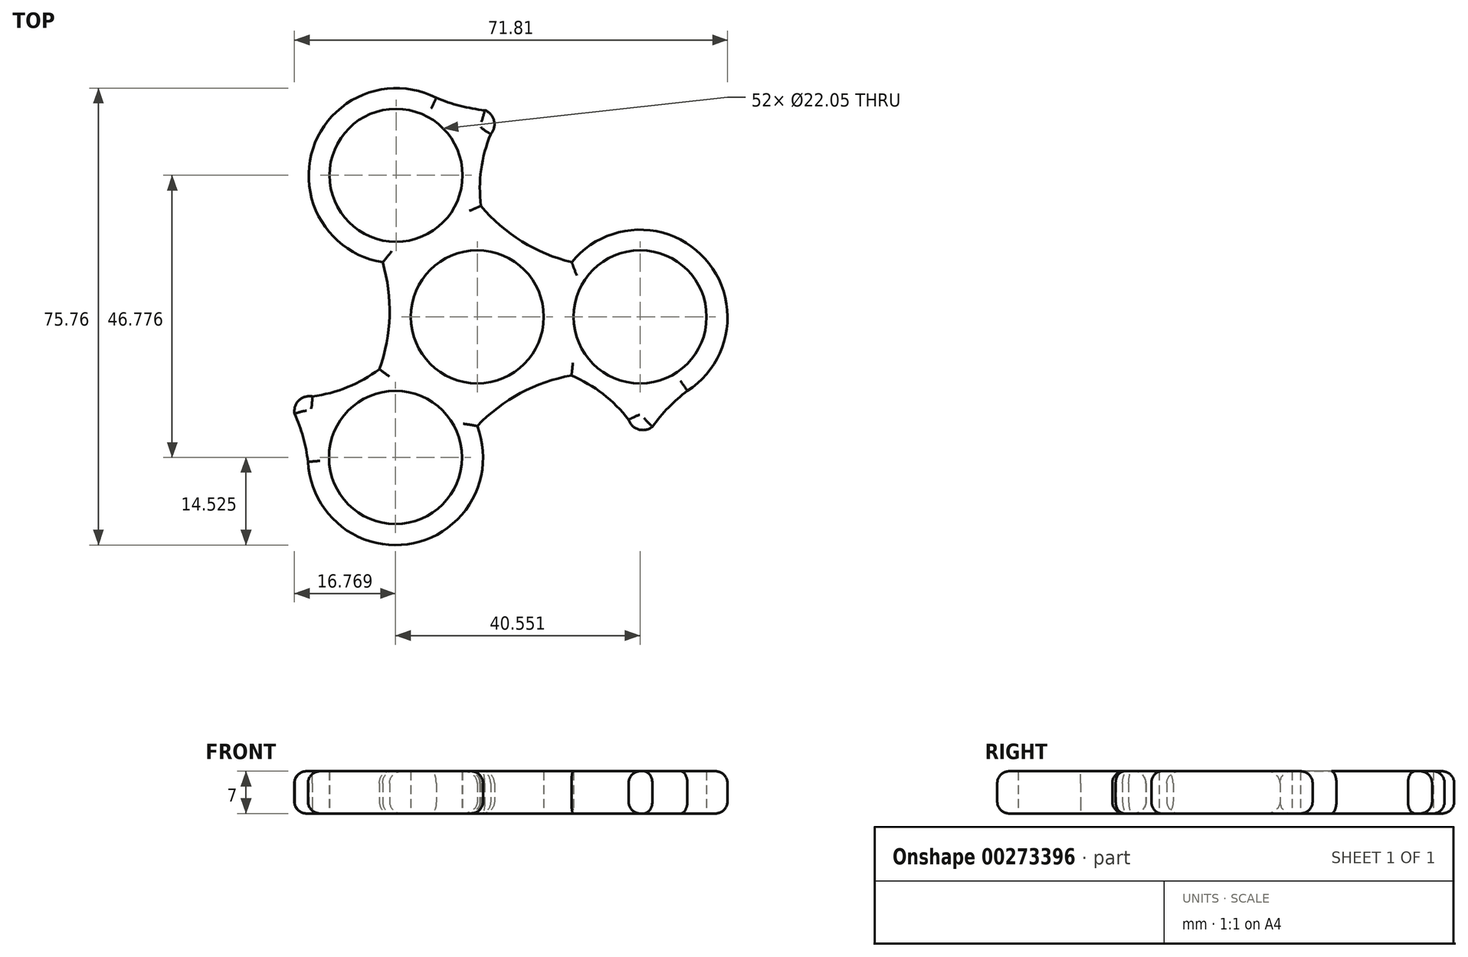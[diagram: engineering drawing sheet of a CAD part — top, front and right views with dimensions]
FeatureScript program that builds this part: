
annotation { "Feature Type Name" : "Feature", "Feature Type Description" : "" }
export const myFeature = defineFeature(function(context is Context, id is Id, definition is map)
    precondition{}
    {
        {
            var Q0;
            Q0=qCreatedBy(makeId("Top.planeOp"),FACE);
            var sketch = newSketch(context, id + "F0", { "sketchPlane" : qUnion([Q0])});
            skCircle(sketch, "E0", {"center": v(0, 0) * mm, "radius": 11.03 * mm});
            skCircle(sketch, "E1", {"center": v(27, 0) * mm, "radius": 11.03 * mm});
            skPoint(sketch, "E2.orphan", {"position": v(-24.95, -16.35) * mm});
            skCircle(sketch, "E3.1.0", {"center": v(-13.47, 23.46) * mm, "radius": 11.03 * mm});
            skCircle(sketch, "E3.2.0", {"center": v(-13.55, -23.31) * mm, "radius": 11.03 * mm});
            skArc(sketch, "E3.2.1", {"start": v(-28.06, -24.04) * mm, "mid": v(-9.44, -37.25) * mm, "end": v(-0.97, -16.05) * mm});
            skArc(sketch, "E3.2.2", {"start": v(-28.06, -24.04) * mm, "mid": v(-28.87, -19.96) * mm, "end": v(-30.29, -16.04) * mm});
            skArc(sketch, "E3.2.3", {"start": v(-27.33, -13.2) * mm, "mid": v(-20.15, -11.06) * mm, "end": v(-14, -6.78) * mm});
            skArc(sketch, "E3.2.4", {"start": v(-27.33, -13.2) * mm, "mid": v(-29.56, -13.85) * mm, "end": v(-30.29, -16.04) * mm});
            skPoint(sketch, "E3.center", {"position": v(0, 0.05) * mm});
            skArc(sketch, "E4.0", {"start": v(-16.23, -8.67) * mm, "mid": v(-14.53, 1.1) * mm, "end": v(-16.28, 10.85) * mm});
            skArc(sketch, "E5.1.0", {"start": v(25.1, -17.07) * mm, "mid": v(26.77, -18.67) * mm, "end": v(29.04, -18.21) * mm});
            skArc(sketch, "E5.1.1", {"start": v(34.85, -12.28) * mm, "mid": v(31.72, -15.03) * mm, "end": v(29.04, -18.21) * mm});
            skArc(sketch, "E5.1.2", {"start": v(34.85, -12.28) * mm, "mid": v(36.98, 10.45) * mm, "end": v(14.38, 7.18) * mm});
            skArc(sketch, "E5.1.3", {"start": v(25.1, -17.07) * mm, "mid": v(19.66, -11.92) * mm, "end": v(12.87, -8.74) * mm});
            skArc(sketch, "E5.1.4", {"start": v(15.63, -9.72) * mm, "mid": v(6.32, -13.13) * mm, "end": v(-1.26, -19.53) * mm});
            skArc(sketch, "E5.2.0", {"start": v(2.23, 30.27) * mm, "mid": v(2.79, 32.52) * mm, "end": v(1.25, 34.25) * mm});
            skArc(sketch, "E5.2.1", {"start": v(-6.8, 36.32) * mm, "mid": v(-2.85, 34.98) * mm, "end": v(1.25, 34.25) * mm});
            skArc(sketch, "E5.2.2", {"start": v(-6.8, 36.32) * mm, "mid": v(-27.54, 26.8) * mm, "end": v(-13.4, 8.87) * mm});
            skArc(sketch, "E5.2.3", {"start": v(2.23, 30.27) * mm, "mid": v(0.5, 22.98) * mm, "end": v(1.14, 15.52) * mm});
            skArc(sketch, "E5.2.4", {"start": v(0.6, 18.4) * mm, "mid": v(8.21, 12.04) * mm, "end": v(17.54, 8.68) * mm});
            skCircle(sketch, "E6", {"center": v(0, 0) * mm, "radius": 41.5 * mm, "construction": true});
            skSolve(sketch);
        }
        {
            var Q0;
            Q0=makeQuery(id+"F0.imprint","IMPRINT",FACE,{"disambiguationData":[TD([[makeQuery(id+"F0.imprint","IMPRINT",EDGE,{"derivedFrom":sQuery(id+"F0.wireOp",EDGE,"E0")}),-1.0]])]});
            extrude(context, id + "F1", {"entities" : qUnion([Q0]), "depth" : 7 * mm});
        }
        {
            var Q0;
            Q0=makeQuery(id+"F1.opExtrude","CAP_EDGE",EDGE,{"disambiguationData":[OSD([sQuery(id+"F0.wireOp",EDGE,"2c41e8ea-b216-4982-985e-4cea36fc87c6.1.2")])],"isStart":true});
            var Q1;
            Q1=makeQuery(id+"F1.opExtrude","CAP_EDGE",EDGE,{"disambiguationData":[OSD([sQuery(id+"F0.wireOp",EDGE,"jCiB0JCp-XQ0B-x5m0-Kedy-DZMXEMae4YiA")])],"isStart":true});
            var Q2;
            Q2=makeQuery(id+"F1.opExtrude","CAP_EDGE",EDGE,{"disambiguationData":[OSD([sQuery(id+"F0.wireOp",EDGE,"8rKnusNR-KdCl-6pd1-ZRWQ-f5KsOQsDNK9e")])],"isStart":true});
            var Q3;
            Q3=makeQuery(id+"F1.opExtrude","CAP_EDGE",EDGE,{"disambiguationData":[OSD([sQuery(id+"F0.wireOp",EDGE,"e85625f6-0f73-4f70-b7ad-6b2c52379fcd.2.0")])],"isStart":true});
            var Q4;
            Q4=makeQuery(id+"F1.opExtrude","CAP_EDGE",EDGE,{"disambiguationData":[OSD([sQuery(id+"F0.wireOp",EDGE,"e85625f6-0f73-4f70-b7ad-6b2c52379fcd.1.0")])],"isStart":true});
            var Q5;
            Q5=makeQuery(id+"F1.opExtrude","CAP_EDGE",EDGE,{"disambiguationData":[OSD([sQuery(id+"F0.wireOp",EDGE,"2c41e8ea-b216-4982-985e-4cea36fc87c6.2.2")])],"isStart":true});
            var Q6;
            Q6=makeQuery(id+"F1.opExtrude","CAP_EDGE",EDGE,{"disambiguationData":[OSD([sQuery(id+"F0.wireOp",EDGE,"jCiB0JCp-XQ0B-x5m0-Kedy-DZMXEMae4YiA")])],"isStart":false});
            var Q7;
            Q7=makeQuery(id+"F1.opExtrude","CAP_EDGE",EDGE,{"disambiguationData":[OSD([sQuery(id+"F0.wireOp",EDGE,"2c41e8ea-b216-4982-985e-4cea36fc87c6.1.2")])],"isStart":false});
            var Q8;
            Q8=makeQuery(id+"F1.opExtrude","CAP_EDGE",EDGE,{"disambiguationData":[OSD([sQuery(id+"F0.wireOp",EDGE,"e85625f6-0f73-4f70-b7ad-6b2c52379fcd.2.0")])],"isStart":false});
            var Q9;
            Q9=makeQuery(id+"F1.opExtrude","CAP_EDGE",EDGE,{"disambiguationData":[OSD([sQuery(id+"F0.wireOp",EDGE,"8rKnusNR-KdCl-6pd1-ZRWQ-f5KsOQsDNK9e")])],"isStart":false});
            var Q10;
            Q10=makeQuery(id+"F1.opExtrude","CAP_EDGE",EDGE,{"disambiguationData":[OSD([sQuery(id+"F0.wireOp",EDGE,"2c41e8ea-b216-4982-985e-4cea36fc87c6.2.2")])],"isStart":false});
            var Q11;
            Q11=makeQuery(id+"F1.opExtrude","CAP_EDGE",EDGE,{"disambiguationData":[OSD([sQuery(id+"F0.wireOp",EDGE,"qkignPZE-vKHs-Vw8X-w2Nq-P10X6wtjNAuJ")])],"isStart":false});
            var Q12;
            Q12=makeQuery(id+"F1.opExtrude","CAP_EDGE",EDGE,{"disambiguationData":[OSD([sQuery(id+"F0.wireOp",EDGE,"a09d2315-2299-4be2-bcc0-b27aebac17a9.1.1")])],"isStart":false});
            var Q13;
            Q13=makeQuery(id+"F1.opExtrude","CAP_EDGE",EDGE,{"disambiguationData":[OSD([sQuery(id+"F0.wireOp",EDGE,"a09d2315-2299-4be2-bcc0-b27aebac17a9.2.1")])],"isStart":false});
            var Q14;
            Q14=makeQuery(id+"F1.opExtrude","CAP_EDGE",EDGE,{"disambiguationData":[OSD([sQuery(id+"F0.wireOp",EDGE,"a09d2315-2299-4be2-bcc0-b27aebac17a9.2.0")])],"isStart":false});
            var Q15;
            Q15=makeQuery(id+"F1.opExtrude","CAP_EDGE",EDGE,{"disambiguationData":[OSD([sQuery(id+"F0.wireOp",EDGE,"7JYrFIuE-K7Xn-0Jy4-bwcr-O0BEukw54Et5")])],"isStart":false});
            var Q16;
            Q16=makeQuery(id+"F1.opExtrude","CAP_EDGE",EDGE,{"disambiguationData":[OSD([sQuery(id+"F0.wireOp",EDGE,"d141c151-67c0-49ed-b5f6-7262cdf8d574.2.2")])],"isStart":false});
            var Q17;
            Q17=makeQuery(id+"F1.opExtrude","CAP_EDGE",EDGE,{"disambiguationData":[OSD([sQuery(id+"F0.wireOp",EDGE,"a09d2315-2299-4be2-bcc0-b27aebac17a9.1.0")])],"isStart":false});
            var Q18;
            Q18=makeQuery(id+"F1.opExtrude","CAP_EDGE",EDGE,{"disambiguationData":[OSD([sQuery(id+"F0.wireOp",EDGE,"vcM62SHT-zkDI-DuHv-aWbG-MSvfoTBMthVj")])],"isStart":false});
            var Q19;
            Q19=makeQuery(id+"F1.opExtrude","CAP_EDGE",EDGE,{"disambiguationData":[OSD([sQuery(id+"F0.wireOp",EDGE,"d141c151-67c0-49ed-b5f6-7262cdf8d574.1.2")])],"isStart":false});
            var Q20;
            Q20=makeQuery(id+"F1.opExtrude","CAP_EDGE",EDGE,{"disambiguationData":[OSD([sQuery(id+"F0.wireOp",EDGE,"e85625f6-0f73-4f70-b7ad-6b2c52379fcd.1.0")])],"isStart":false});
            var Q21;
            Q21=makeQuery(id+"F1.opExtrude","CAP_EDGE",EDGE,{"disambiguationData":[OSD([sQuery(id+"F0.wireOp",EDGE,"7JYrFIuE-K7Xn-0Jy4-bwcr-O0BEukw54Et5")])],"isStart":true});
            var Q22;
            Q22=makeQuery(id+"F1.opExtrude","CAP_EDGE",EDGE,{"disambiguationData":[OSD([sQuery(id+"F0.wireOp",EDGE,"qkignPZE-vKHs-Vw8X-w2Nq-P10X6wtjNAuJ")])],"isStart":true});
            var Q23;
            Q23=makeQuery(id+"F1.opExtrude","CAP_EDGE",EDGE,{"disambiguationData":[OSD([sQuery(id+"F0.wireOp",EDGE,"a09d2315-2299-4be2-bcc0-b27aebac17a9.2.0")])],"isStart":true});
            var Q24;
            Q24=makeQuery(id+"F1.opExtrude","CAP_EDGE",EDGE,{"disambiguationData":[OSD([sQuery(id+"F0.wireOp",EDGE,"a09d2315-2299-4be2-bcc0-b27aebac17a9.2.1")])],"isStart":true});
            var Q25;
            Q25=makeQuery(id+"F1.opExtrude","CAP_EDGE",EDGE,{"disambiguationData":[OSD([sQuery(id+"F0.wireOp",EDGE,"a09d2315-2299-4be2-bcc0-b27aebac17a9.1.1")])],"isStart":true});
            var Q26;
            Q26=makeQuery(id+"F1.opExtrude","CAP_EDGE",EDGE,{"disambiguationData":[OSD([sQuery(id+"F0.wireOp",EDGE,"a09d2315-2299-4be2-bcc0-b27aebac17a9.1.0")])],"isStart":true});
            var Q27;
            Q27=makeQuery(id+"F1.opExtrude","CAP_EDGE",EDGE,{"disambiguationData":[OSD([sQuery(id+"F0.wireOp",EDGE,"vcM62SHT-zkDI-DuHv-aWbG-MSvfoTBMthVj")])],"isStart":true});
            var Q28;
            Q28=makeQuery(id+"F1.opExtrude","CAP_EDGE",EDGE,{"disambiguationData":[OSD([sQuery(id+"F0.wireOp",EDGE,"EyXljZKZ-RbeY-ZyGO-U8lE-6hOu3Im0BXS0")])],"isStart":true});
            var Q29;
            Q29=makeQuery(id+"F1.opExtrude","CAP_EDGE",EDGE,{"disambiguationData":[OSD([sQuery(id+"F0.wireOp",EDGE,"247ecdd3-580a-4f05-8964-3e7654aa62d4.1.0")])],"isStart":true});
            var Q30;
            Q30=makeQuery(id+"F1.opExtrude","CAP_EDGE",EDGE,{"disambiguationData":[OSD([sQuery(id+"F0.wireOp",EDGE,"247ecdd3-580a-4f05-8964-3e7654aa62d4.2.0")])],"isStart":true});
            var Q31;
            Q31=makeQuery(id+"F1.opExtrude","CAP_EDGE",EDGE,{"disambiguationData":[OSD([sQuery(id+"F0.wireOp",EDGE,"247ecdd3-580a-4f05-8964-3e7654aa62d4.2.0")])],"isStart":false});
            var Q32;
            Q32=makeQuery(id+"F1.opExtrude","CAP_EDGE",EDGE,{"disambiguationData":[OSD([sQuery(id+"F0.wireOp",EDGE,"EyXljZKZ-RbeY-ZyGO-U8lE-6hOu3Im0BXS0")])],"isStart":false});
            var Q33;
            Q33=makeQuery(id+"F1.opExtrude","CAP_EDGE",EDGE,{"disambiguationData":[OSD([sQuery(id+"F0.wireOp",EDGE,"247ecdd3-580a-4f05-8964-3e7654aa62d4.1.0")])],"isStart":false});
            var Q34;
            Q34=makeQuery(id+"F1.opExtrude","CAP_EDGE",EDGE,{"disambiguationData":[OSD([sQuery(id+"F0.wireOp",EDGE,"ed2d72a4-419b-47cf-ace9-9678367d7267.2.0")])],"isStart":false});
            var Q35;
            Q35=makeQuery(id+"F1.opExtrude","CAP_EDGE",EDGE,{"disambiguationData":[OSD([sQuery(id+"F0.wireOp",EDGE,"ed2d72a4-419b-47cf-ace9-9678367d7267.1.0")])],"isStart":false});
            var Q36;
            Q36=makeQuery(id+"F1.opExtrude","CAP_EDGE",EDGE,{"disambiguationData":[OSD([sQuery(id+"F0.wireOp",EDGE,"ed2d72a4-419b-47cf-ace9-9678367d7267.1.1")])],"isStart":false});
            var Q37;
            Q37=makeQuery(id+"F1.opExtrude","CAP_EDGE",EDGE,{"disambiguationData":[OSD([sQuery(id+"F0.wireOp",EDGE,"weM6L15f-GAZl-oho3-8Uek-PDMmfMEMd7Oe")])],"isStart":false});
            var Q38;
            Q38=makeQuery(id+"F1.opExtrude","CAP_EDGE",EDGE,{"disambiguationData":[OSD([sQuery(id+"F0.wireOp",EDGE,"ed2d72a4-419b-47cf-ace9-9678367d7267.2.2")])],"isStart":false});
            var Q39;
            Q39=makeQuery(id+"F1.opExtrude","CAP_EDGE",EDGE,{"disambiguationData":[OSD([sQuery(id+"F0.wireOp",EDGE,"ed2d72a4-419b-47cf-ace9-9678367d7267.1.1")])],"isStart":true});
            var Q40;
            Q40=makeQuery(id+"F1.opExtrude","CAP_EDGE",EDGE,{"disambiguationData":[OSD([sQuery(id+"F0.wireOp",EDGE,"ed2d72a4-419b-47cf-ace9-9678367d7267.1.0")])],"isStart":true});
            var Q41;
            Q41=makeQuery(id+"F1.opExtrude","CAP_EDGE",EDGE,{"disambiguationData":[OSD([sQuery(id+"F0.wireOp",EDGE,"ed2d72a4-419b-47cf-ace9-9678367d7267.1.2")])],"isStart":true});
            var Q42;
            Q42=makeQuery(id+"F1.opExtrude","CAP_EDGE",EDGE,{"disambiguationData":[OSD([sQuery(id+"F0.wireOp",EDGE,"weM6L15f-GAZl-oho3-8Uek-PDMmfMEMd7Oe")])],"isStart":true});
            var Q43;
            Q43=makeQuery(id+"F1.opExtrude","CAP_EDGE",EDGE,{"disambiguationData":[OSD([sQuery(id+"F0.wireOp",EDGE,"ed2d72a4-419b-47cf-ace9-9678367d7267.2.0")])],"isStart":true});
            var Q44;
            Q44=makeQuery(id+"F1.opExtrude","CAP_EDGE",EDGE,{"disambiguationData":[OSD([sQuery(id+"F0.wireOp",EDGE,"ed2d72a4-419b-47cf-ace9-9678367d7267.2.2")])],"isStart":true});
            var Q45;
            Q45=makeQuery(id+"F1.opExtrude","CAP_EDGE",EDGE,{"disambiguationData":[OSD([sQuery(id+"F0.wireOp",EDGE,"ed2d72a4-419b-47cf-ace9-9678367d7267.1.2")])],"isStart":false});
            var Q46;
            Q46=makeQuery(id+"F1.opExtrude","CAP_EDGE",EDGE,{"disambiguationData":[OSD([sQuery(id+"F0.wireOp",EDGE,"E3.1.1")])],"isStart":true});
            var Q47;
            Q47=makeQuery(id+"F1.opExtrude","CAP_EDGE",EDGE,{"disambiguationData":[OSD([sQuery(id+"F0.wireOp",EDGE,"E3.1.3")])],"isStart":true});
            var Q48;
            Q48=makeQuery(id+"F1.opExtrude","CAP_EDGE",EDGE,{"disambiguationData":[OSD([sQuery(id+"F0.wireOp",EDGE,"E3.1.4")])],"isStart":true});
            var Q49;
            Q49=makeQuery(id+"F1.opExtrude","CAP_EDGE",EDGE,{"disambiguationData":[OSD([sQuery(id+"F0.wireOp",EDGE,"E3.2.3")])],"isStart":true});
            var Q50;
            Q50=makeQuery(id+"F1.opExtrude","CAP_EDGE",EDGE,{"disambiguationData":[OSD([sQuery(id+"F0.wireOp",EDGE,"E3.2.4")])],"isStart":true});
            var Q51;
            Q51=makeQuery(id+"F1.opExtrude","CAP_EDGE",EDGE,{"disambiguationData":[OSD([sQuery(id+"F0.wireOp",EDGE,"E3.2.2")])],"isStart":true});
            var Q52;
            Q52=makeQuery(id+"F1.opExtrude","CAP_EDGE",EDGE,{"disambiguationData":[OSD([sQuery(id+"F0.wireOp",EDGE,"E3.2.1")])],"isStart":true});
            var Q53;
            Q53=makeQuery(id+"F1.opExtrude","CAP_EDGE",EDGE,{"disambiguationData":[OSD([sQuery(id+"F0.wireOp",EDGE,"E3.2.1")])],"isStart":false});
            var Q54;
            Q54=makeQuery(id+"F1.opExtrude","CAP_EDGE",EDGE,{"disambiguationData":[OSD([sQuery(id+"F0.wireOp",EDGE,"E3.2.3")])],"isStart":false});
            var Q55;
            Q55=makeQuery(id+"F1.opExtrude","CAP_EDGE",EDGE,{"disambiguationData":[OSD([sQuery(id+"F0.wireOp",EDGE,"E3.2.4")])],"isStart":false});
            var Q56;
            Q56=makeQuery(id+"F1.opExtrude","CAP_EDGE",EDGE,{"disambiguationData":[OSD([sQuery(id+"F0.wireOp",EDGE,"E3.1.1")])],"isStart":false});
            var Q57;
            Q57=makeQuery(id+"F1.opExtrude","CAP_EDGE",EDGE,{"disambiguationData":[OSD([sQuery(id+"F0.wireOp",EDGE,"E3.1.2")])],"isStart":false});
            var Q58;
            Q58=makeQuery(id+"F1.opExtrude","CAP_EDGE",EDGE,{"disambiguationData":[OSD([sQuery(id+"F0.wireOp",EDGE,"E3.1.3")])],"isStart":false});
            var Q59;
            Q59=makeQuery(id+"F1.opExtrude","CAP_EDGE",EDGE,{"disambiguationData":[OSD([sQuery(id+"F0.wireOp",EDGE,"E3.1.4")])],"isStart":false});
            var Q60;
            Q60=makeQuery(id+"F1.opExtrude","CAP_EDGE",EDGE,{"disambiguationData":[OSD([sQuery(id+"F0.wireOp",EDGE,"E4.0")])],"isStart":false});
            var Q61;
            Q61=makeQuery(id+"F1.opExtrude","CAP_EDGE",EDGE,{"disambiguationData":[OSD([sQuery(id+"F0.wireOp",EDGE,"E5.2.2")])],"isStart":false});
            var Q62;
            Q62=makeQuery(id+"F1.opExtrude","CAP_EDGE",EDGE,{"disambiguationData":[OSD([sQuery(id+"F0.wireOp",EDGE,"E5.2.3")])],"isStart":false});
            var Q63;
            Q63=makeQuery(id+"F1.opExtrude","CAP_EDGE",EDGE,{"disambiguationData":[OSD([sQuery(id+"F0.wireOp",EDGE,"E5.2.4")])],"isStart":false});
            var Q64;
            Q64=makeQuery(id+"F1.opExtrude","CAP_EDGE",EDGE,{"disambiguationData":[OSD([sQuery(id+"F0.wireOp",EDGE,"E5.1.2")])],"isStart":false});
            var Q65;
            Q65=makeQuery(id+"F1.opExtrude","CAP_EDGE",EDGE,{"disambiguationData":[OSD([sQuery(id+"F0.wireOp",EDGE,"E5.1.4")])],"isStart":false});
            var Q66;
            Q66=makeQuery(id+"F1.opExtrude","CAP_EDGE",EDGE,{"disambiguationData":[OSD([sQuery(id+"F0.wireOp",EDGE,"E5.1.3")])],"isStart":false});
            var Q67;
            Q67=makeQuery(id+"F1.opExtrude","CAP_EDGE",EDGE,{"disambiguationData":[OSD([sQuery(id+"F0.wireOp",EDGE,"E5.1.0")])],"isStart":false});
            var Q68;
            Q68=makeQuery(id+"F1.opExtrude","CAP_EDGE",EDGE,{"disambiguationData":[OSD([sQuery(id+"F0.wireOp",EDGE,"E5.2.0")])],"isStart":false});
            var Q69;
            Q69=makeQuery(id+"F1.opExtrude","CAP_EDGE",EDGE,{"disambiguationData":[OSD([sQuery(id+"F0.wireOp",EDGE,"E4.0")])],"isStart":true});
            var Q70;
            Q70=makeQuery(id+"F1.opExtrude","CAP_EDGE",EDGE,{"disambiguationData":[OSD([sQuery(id+"F0.wireOp",EDGE,"E5.2.2")])],"isStart":true});
            var Q71;
            Q71=makeQuery(id+"F1.opExtrude","CAP_EDGE",EDGE,{"disambiguationData":[OSD([sQuery(id+"F0.wireOp",EDGE,"E5.1.4")])],"isStart":true});
            var Q72;
            Q72=makeQuery(id+"F1.opExtrude","CAP_EDGE",EDGE,{"disambiguationData":[OSD([sQuery(id+"F0.wireOp",EDGE,"E5.1.0")])],"isStart":true});
            var Q73;
            Q73=makeQuery(id+"F1.opExtrude","CAP_EDGE",EDGE,{"disambiguationData":[OSD([sQuery(id+"F0.wireOp",EDGE,"E5.1.3")])],"isStart":true});
            var Q74;
            Q74=makeQuery(id+"F1.opExtrude","CAP_EDGE",EDGE,{"disambiguationData":[OSD([sQuery(id+"F0.wireOp",EDGE,"E5.1.2")])],"isStart":true});
            var Q75;
            Q75=makeQuery(id+"F1.opExtrude","CAP_EDGE",EDGE,{"disambiguationData":[OSD([sQuery(id+"F0.wireOp",EDGE,"E5.2.4")])],"isStart":true});
            var Q76;
            Q76=makeQuery(id+"F1.opExtrude","CAP_EDGE",EDGE,{"disambiguationData":[OSD([sQuery(id+"F0.wireOp",EDGE,"E5.2.0")])],"isStart":true});
            var Q77;
            Q77=makeQuery(id+"F1.opExtrude","CAP_EDGE",EDGE,{"disambiguationData":[OSD([sQuery(id+"F0.wireOp",EDGE,"E5.2.3")])],"isStart":true});
            var Q78;
            Q78=makeQuery(id+"F1.opExtrude","CAP_EDGE",EDGE,{"disambiguationData":[OSD([sQuery(id+"F0.wireOp",EDGE,"E5.2.1")])],"isStart":true});
            fillet(context, id + "F2", {"entities" : qUnion([Q0, Q1, Q2, Q3, Q4, Q5, Q6, Q7, Q8, Q9, Q10, Q11, Q12, Q13, Q14, Q15, Q16, Q17, Q18, Q19, Q20, Q21, Q22, Q23, Q24, Q25, Q26, Q27, Q28, Q29, Q30, Q31, Q32, Q33, Q34, Q35, Q36, Q37, Q38, Q39, Q40, Q41, Q42, Q43, Q44, Q45, Q46, Q47, Q48, Q49, Q50, Q51, Q52, Q53, Q54, Q55, Q56, Q57, Q58, Q59, Q60, Q61, Q62, Q63, Q64, Q65, Q66, Q67, Q68, Q69, Q70, Q71, Q72, Q73, Q74, Q75, Q76, Q77, Q78]), "radius" : 2 * mm, "tangentPropagation" : true, "allowEdgeOverflow" : false});
        }
    });
